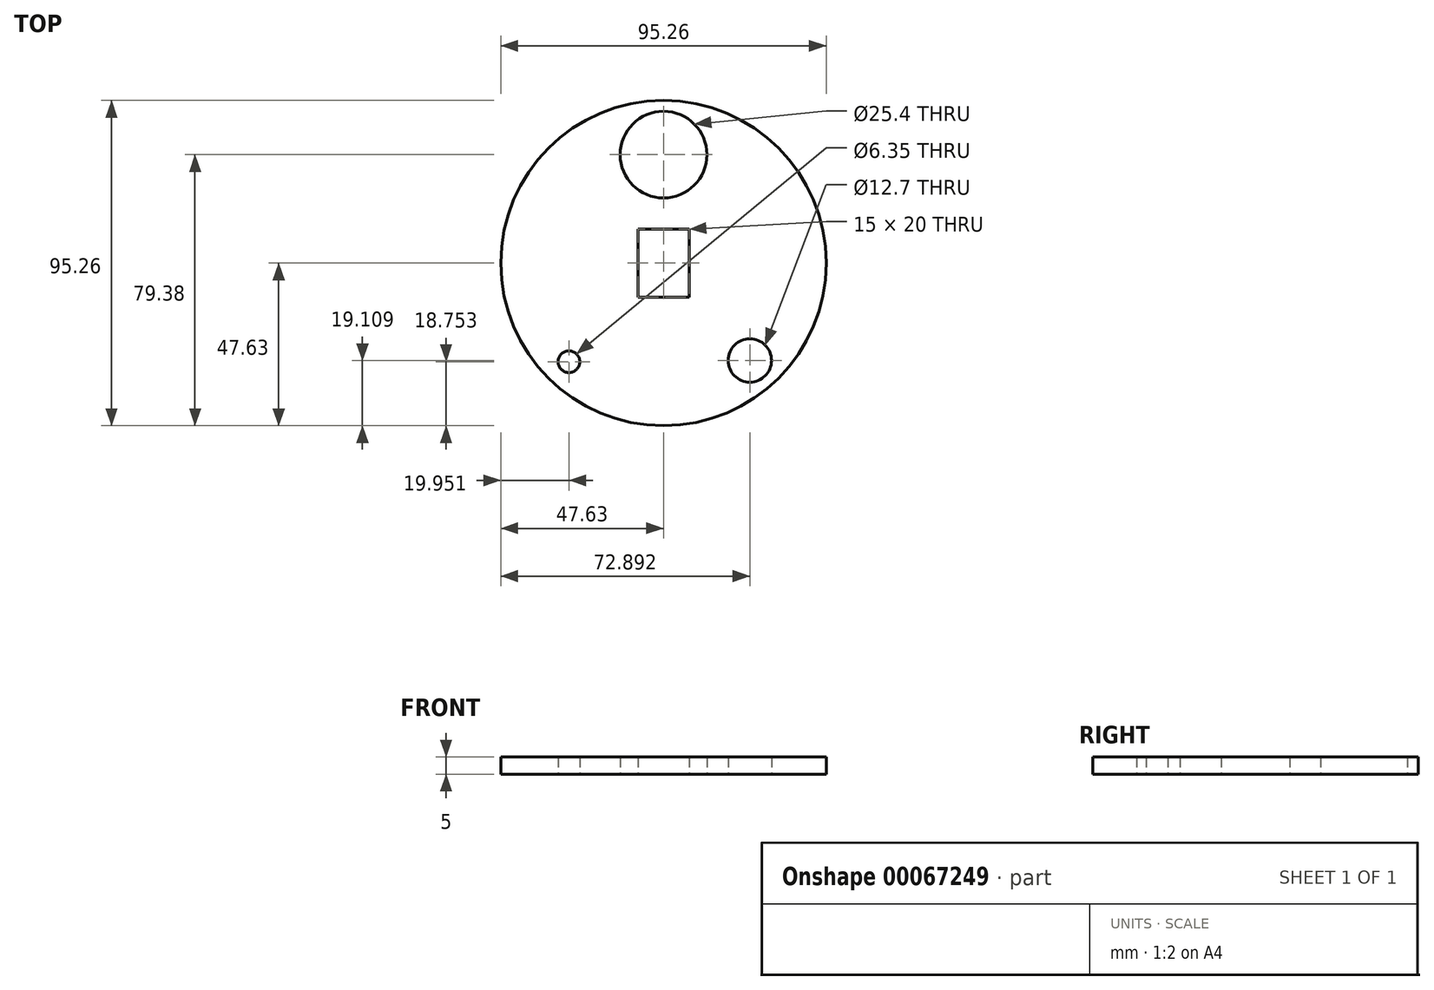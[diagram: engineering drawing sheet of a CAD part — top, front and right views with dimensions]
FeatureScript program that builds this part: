
annotation { "Feature Type Name" : "Feature", "Feature Type Description" : "" }
export const myFeature = defineFeature(function(context is Context, id is Id, definition is map)
    precondition{}
    {
        {
            var Q0;
            Q0=qCreatedBy(makeId("Top.planeOp"),FACE);
            var sketch = newSketch(context, id + "F0", { "sketchPlane" : qUnion([Q0])});
            skCircle(sketch, "E0", {"center": v(0, 0) * mm, "radius": 47.63 * mm});
            skLineSegment(sketch, "E1.bottom", {"start": v(-7.5, 10) * mm, "end": v(7.5, 10) * mm});
            skLineSegment(sketch, "E1.top", {"start": v(-7.5, -10) * mm, "end": v(7.5, -10) * mm});
            skLineSegment(sketch, "E1.left", {"start": v(-7.5, 10) * mm, "end": v(-7.5, -10) * mm});
            skLineSegment(sketch, "E1.right", {"start": v(7.5, 10) * mm, "end": v(7.5, -10) * mm});
            skCircle(sketch, "E2", {"center": v(0, 31.75) * mm, "radius": 12.7 * mm});
            skCircle(sketch, "E3", {"center": v(-27.68, -28.88) * mm, "radius": 3.18 * mm});
            skCircle(sketch, "E4", {"center": v(25.26, -28.52) * mm, "radius": 6.35 * mm});
            skSolve(sketch);
        }
        {
            var Q0;
            Q0=qSketchRegion(id+"F0",true);
            extrude(context, id + "F1", {"entities" : qUnion([Q0]), "depth" : 5 * mm});
        }
    });
